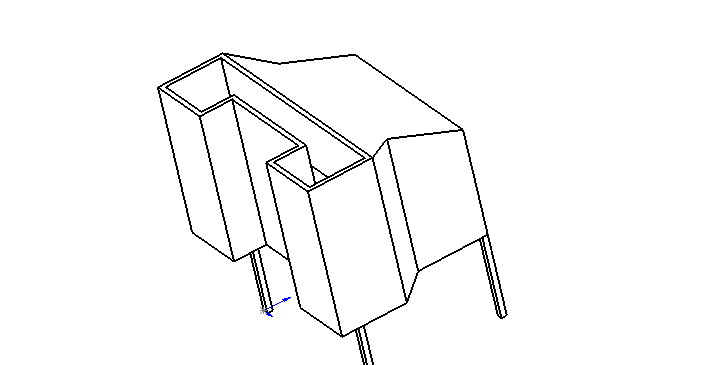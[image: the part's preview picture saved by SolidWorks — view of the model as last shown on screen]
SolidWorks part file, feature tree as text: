
SOLIDWORKS PART (.sldprt)
format: sldprt  version: not decoded by parser v0  size: 347,136 bytes
history: native  units: mm
features: sketch x4, extrude x2, cut_extrude x2, shell x1 (+11 scaffold rows collapsed)
feature tree (20):
  scaffold x11  (default folders/planes/origin — collapsed)
  sketch  "Sketch1"  dims[c1.D1=101.6mm c1.D2=101.6mm c2.D1=101.6mm c2.D2=101.6mm c2.D3=90.0deg c2.D4=2438.4mm]
  extrude  "Extrude1"  Depth=1524mm
  sketch  "Sketch24"  dims[c1.D1=1219.2mm c1.D2=1219.2mm c1.D3=1219.2mm c1.D4=1219.2mm c1.D5=609.6mm c1.D6=609.6mm c1.D7=609.6mm c1.D8=609.6mm c2.D3=609.6mm c3.D3=45.0deg c3.D9=~869.33348mm c4.D9=45.0deg c4.D3=1219.2mm c5.D3=45.0deg c5.D9=1219.2mm c6.D9=45.0deg]
  extrude  "Extrude2"  Depth=2743.2mm
  sketch  "Sketch25"  dims[D1=762.0mm]
  cut_extrude  "Cut-Extrude16"  [1 undecoded]
  sketch  "Sketch26"  dims[D1=88.9mm]
  cut_extrude  "Cut-Extrude17"  Depth=1016mm
  shell  "Shell5"  Thickness=88.9mm
decode coverage: 8 of 9 modeling features carry decoded parameters
note: ~ marks probable driven/reference dimensions
note: 1 parameter value undecoded
note: suppression state not decoded; provenance and decode notes live in map.json
